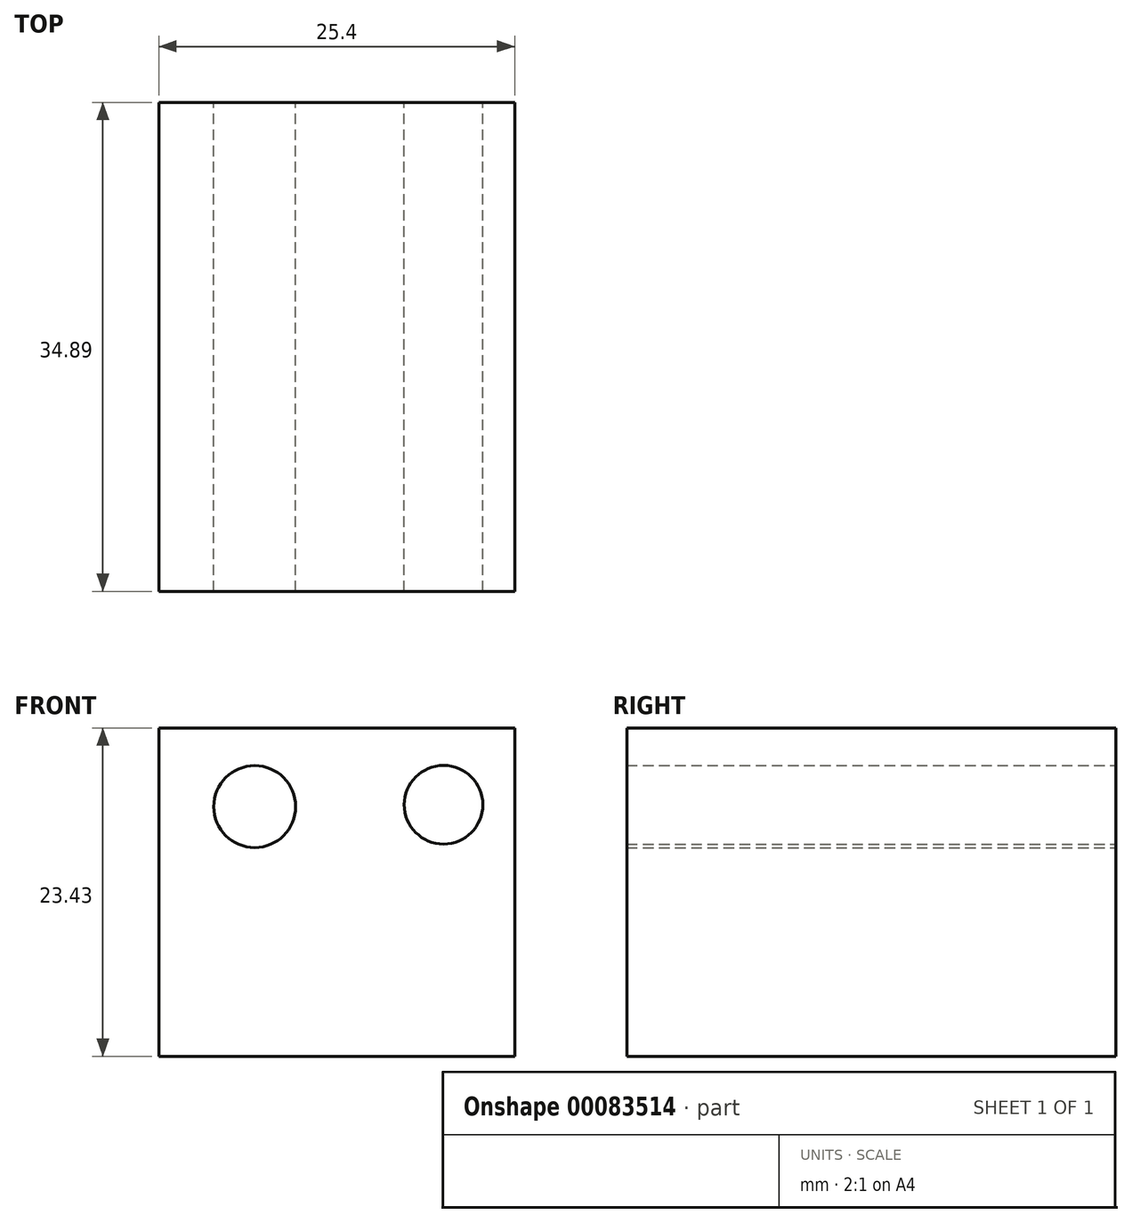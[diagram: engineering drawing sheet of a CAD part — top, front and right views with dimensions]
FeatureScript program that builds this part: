
annotation { "Feature Type Name" : "Feature", "Feature Type Description" : "" }
export const myFeature = defineFeature(function(context is Context, id is Id, definition is map)
    precondition{}
    {
        {
            var Q0;
            Q0=qCreatedBy(makeId("Right.planeOp"),FACE);
            var sketch = newSketch(context, id + "F0", { "sketchPlane" : qUnion([Q0])});
            skLineSegment(sketch, "E0.bottom", {"start": v(34.9, 23.43) * mm, "end": v(0, 23.43) * mm});
            skLineSegment(sketch, "E0.top", {"start": v(34.9, 0) * mm, "end": v(0, 0) * mm});
            skLineSegment(sketch, "E0.left", {"start": v(34.9, 23.43) * mm, "end": v(34.9, 0) * mm});
            skLineSegment(sketch, "E0.right", {"start": v(0, 23.43) * mm, "end": v(0, 0) * mm});
            skSolve(sketch);
        }
        {
            var Q0;
            Q0=makeQuery(id+"F0.imprint","IMPRINT",FACE,{"disambiguationData":[TD([[makeQuery(id+"F0.imprint","IMPRINT",EDGE,{"derivedFrom":sQuery(id+"F0.wireOp",EDGE,"E0.bottom")}),1.0]])]});
            extrude(context, id + "F1", {"entities" : qUnion([Q0]), "depth" : 25.4 * mm});
        }
        {
            var Q0;
            Q0=makeQuery(id+"F1.opExtrude","SWEPT_FACE",FACE,{"disambiguationData":[OSD([sQuery(id+"F0.wireOp",EDGE,"E0.left")])]});
            var sketch = newSketch(context, id + "F2", { "sketchPlane" : qUnion([Q0])});
            skCircle(sketch, "E1", {"center": v(-20.32, 17.95) * mm, "radius": 2.8 * mm});
            skCircle(sketch, "E2", {"center": v(-6.84, 17.81) * mm, "radius": 2.92 * mm});
            skSolve(sketch);
        }
        {
            var Q0;
            Q0 = qSketchRegion(id + "F2", true);
            extrude(context, id + "F3", {"entities" : qUnion([Q0]), "operationType" : NewBodyOperationType.REMOVE, "endBound" : BoundingType.THROUGH_ALL, "oppositeDirection" : true, "depth" : 25.4 * mm});
        }
    });
